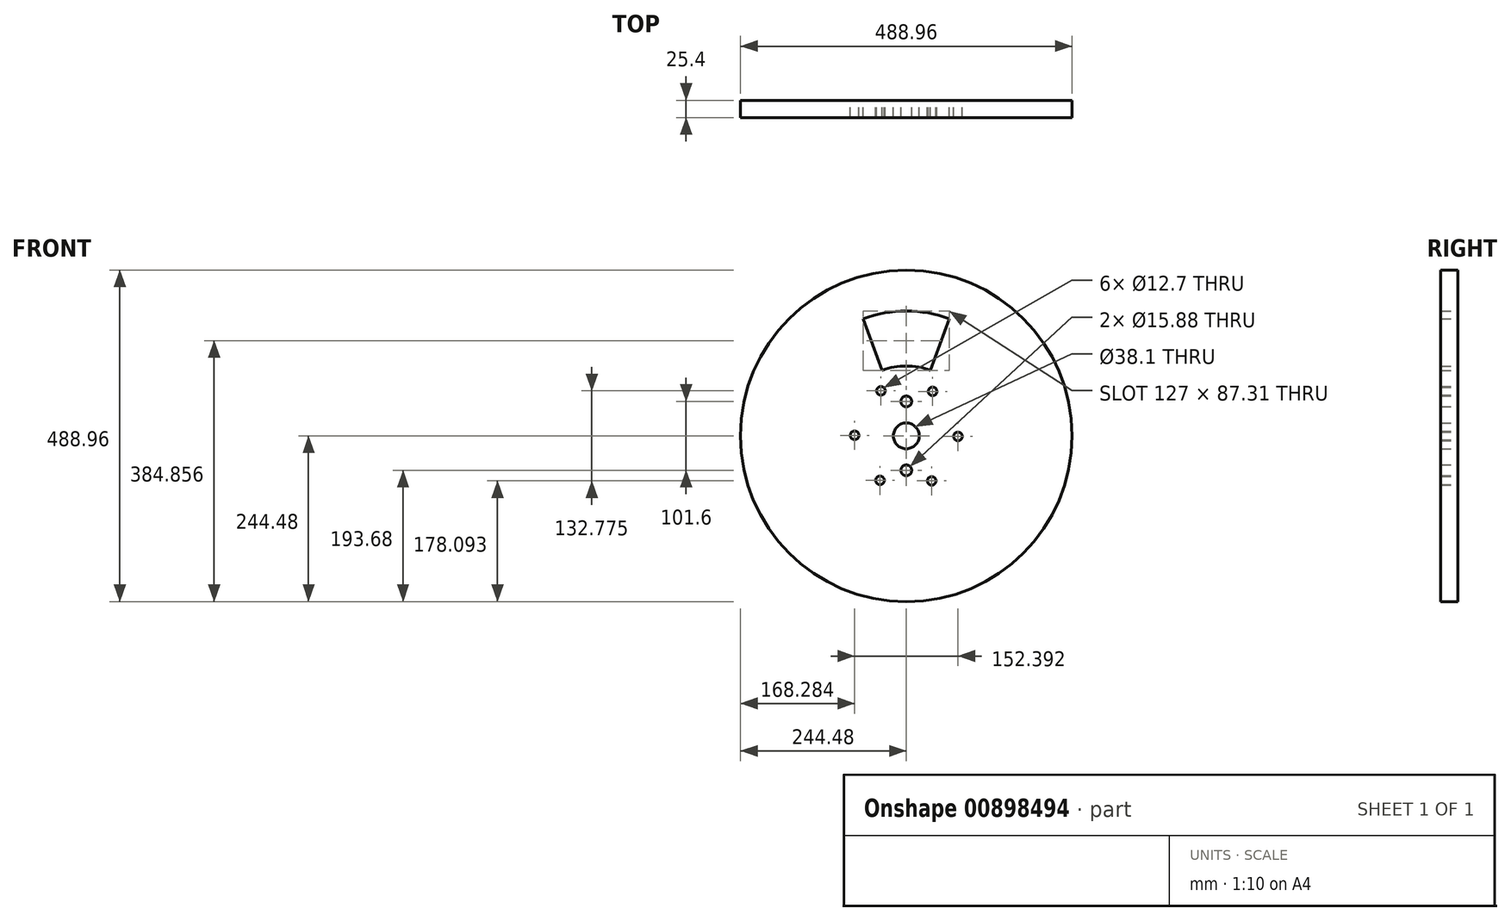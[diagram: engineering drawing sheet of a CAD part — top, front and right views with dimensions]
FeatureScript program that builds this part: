
annotation { "Feature Type Name" : "Feature", "Feature Type Description" : "" }
export const myFeature = defineFeature(function(context is Context, id is Id, definition is map)
    precondition{}
    {
        {
            var Q0;
            Q0=qCreatedBy(makeId("Front.planeOp"),FACE);
            var sketch = newSketch(context, id + "F0", { "sketchPlane" : qUnion([Q0])});
            skCircle(sketch, "E0", {"center": v(0, 0) * mm, "radius": 244.48 * mm});
            skCircle(sketch, "E1", {"center": v(0, 50.8) * mm, "radius": 7.94 * mm});
            skCircle(sketch, "E2", {"center": v(0, -50.8) * mm, "radius": 7.94 * mm});
            skCircle(sketch, "E3", {"center": v(-37.4, 66.39) * mm, "radius": 6.35 * mm});
            skCircle(sketch, "E4", {"center": v(38.8, 65.59) * mm, "radius": 6.35 * mm});
            skCircle(sketch, "E5", {"center": v(76.2, -0.8) * mm, "radius": 6.35 * mm});
            skCircle(sketch, "E6", {"center": v(37.4, -66.39) * mm, "radius": 6.35 * mm});
            skCircle(sketch, "E7", {"center": v(-38.8, -65.59) * mm, "radius": 6.35 * mm});
            skCircle(sketch, "E8", {"center": v(-76.2, 0.8) * mm, "radius": 6.35 * mm});
            skCircle(sketch, "E9", {"center": v(0, 0) * mm, "radius": 19.05 * mm});
            skSolve(sketch);
        }
        {
            var Q0;
            Q0=makeQuery(id+"F0.imprint","IMPRINT",FACE,{"disambiguationData":[TD([[makeQuery(id+"F0.imprint","IMPRINT",EDGE,{"derivedFrom":sQuery(id+"F0.wireOp",EDGE,"E0")}),1.0]])]});
            extrude(context, id + "F1", {"entities" : qUnion([Q0]), "depth" : 25.4 * mm, "offsetDistance" : 25.4 * mm});
        }
        {
            var Q0;
            Q0=qCreatedBy(makeId("Front.planeOp"),FACE);
            var sketch = newSketch(context, id + "F2", { "sketchPlane" : qUnion([Q0])});
            skArc(sketch, "E10", {"start": v(35.56, 96.72) * mm, "mid": v(0, 103.05) * mm, "end": v(-35.56, 96.72) * mm});
            skArc(sketch, "E11", {"start": v(63.5, 172.73) * mm, "mid": v(0, 184.03) * mm, "end": v(-63.5, 172.73) * mm});
            skLineSegment(sketch, "E12", {"start": v(-35.56, 96.72) * mm, "end": v(-63.5, 172.73) * mm});
            skLineSegment(sketch, "E13", {"start": v(35.56, 96.72) * mm, "end": v(63.5, 172.73) * mm});
            skPoint(sketch, "E14.end.orphan", {"position": v(0, 172.73) * mm});
            skSolve(sketch);
        }
        {
            var Q0;
            Q0=makeQuery(id+"F2.imprint","IMPRINT",FACE,{"disambiguationData":[TD([[makeQuery(id+"F2.imprint","IMPRINT",EDGE,{"derivedFrom":sQuery(id+"F2.wireOp",EDGE,"E10")}),-1.0]])]});
            extrude(context, id + "F3", {"entities" : qUnion([Q0]), "operationType" : NewBodyOperationType.REMOVE, "endBound" : BoundingType.UP_TO_NEXT, "depth" : 25.4 * mm, "offsetDistance" : 25.4 * mm});
        }
    });
